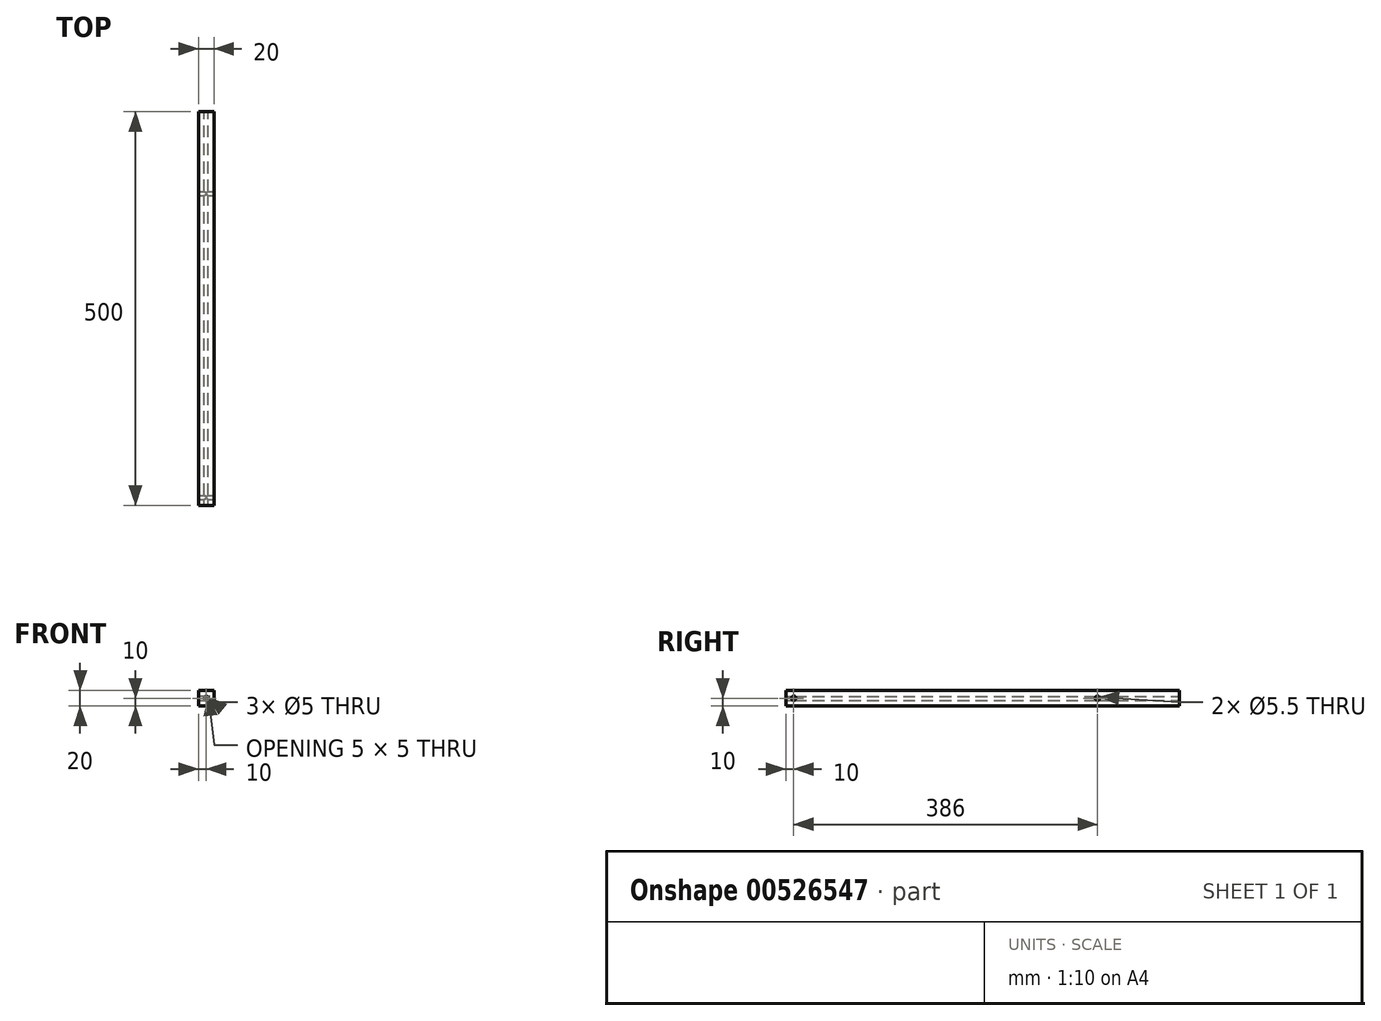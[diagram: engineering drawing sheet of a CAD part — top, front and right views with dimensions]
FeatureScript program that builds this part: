
annotation { "Feature Type Name" : "Feature", "Feature Type Description" : "" }
export const myFeature = defineFeature(function(context is Context, id is Id, definition is map)
    precondition{}
    {
        {
            var Q0;
            Q0=qCreatedBy(makeId("Front.planeOp"),FACE);
            var sketch = newSketch(context, id + "F0", { "sketchPlane" : qUnion([Q0])});
            skLineSegment(sketch, "E0.bottom", {"start": v(-10, 10) * mm, "end": v(10, 10) * mm});
            skLineSegment(sketch, "E0.top", {"start": v(-10, -10) * mm, "end": v(10, -10) * mm});
            skLineSegment(sketch, "E0.left", {"start": v(-10, 10) * mm, "end": v(-10, -10) * mm});
            skLineSegment(sketch, "E0.right", {"start": v(10, 10) * mm, "end": v(10, -10) * mm});
            skPoint(sketch, "E0.middle", {"position": v(0, 0) * mm});
            skCircle(sketch, "E1", {"center": v(0, 0) * mm, "radius": 2.5 * mm});
            skSolve(sketch);
        }
        {
            var Q0;
            Q0 = qSketchRegion(id + "F0", true);
            extrude(context, id + "F1", {"entities" : qUnion([Q0]), "endBound" : BoundingType.SYMMETRIC, "depth" : 500 * mm, "offsetDistance" : 25 * mm});
        }
        {
            var Q0;
            Q0=makeQuery(id+"F1.opExtrude","SWEPT_FACE",FACE,{"disambiguationData":[OSD([sQuery(id+"F0.wireOp",EDGE,"E0.right")])]});
            var sketch = newSketch(context, id + "F2", { "sketchPlane" : qUnion([Q0])});
            skCircle(sketch, "E2", {"center": v(-240, 0) * mm, "radius": 2.75 * mm});
            skPoint(sketch, "E2.centerSnap0", {"position": v(-250, 0) * mm});
            skCircle(sketch, "E3", {"center": v(146, 0) * mm, "radius": 2.75 * mm});
            skSolve(sketch);
        }
        {
            var Q0;
            Q0 = qSketchRegion(id + "F2", true);
            extrude(context, id + "F3", {"entities" : qUnion([Q0]), "operationType" : NewBodyOperationType.REMOVE, "oppositeDirection" : true, "depth" : 20 * mm, "offsetDistance" : 25 * mm});
        }
    });
